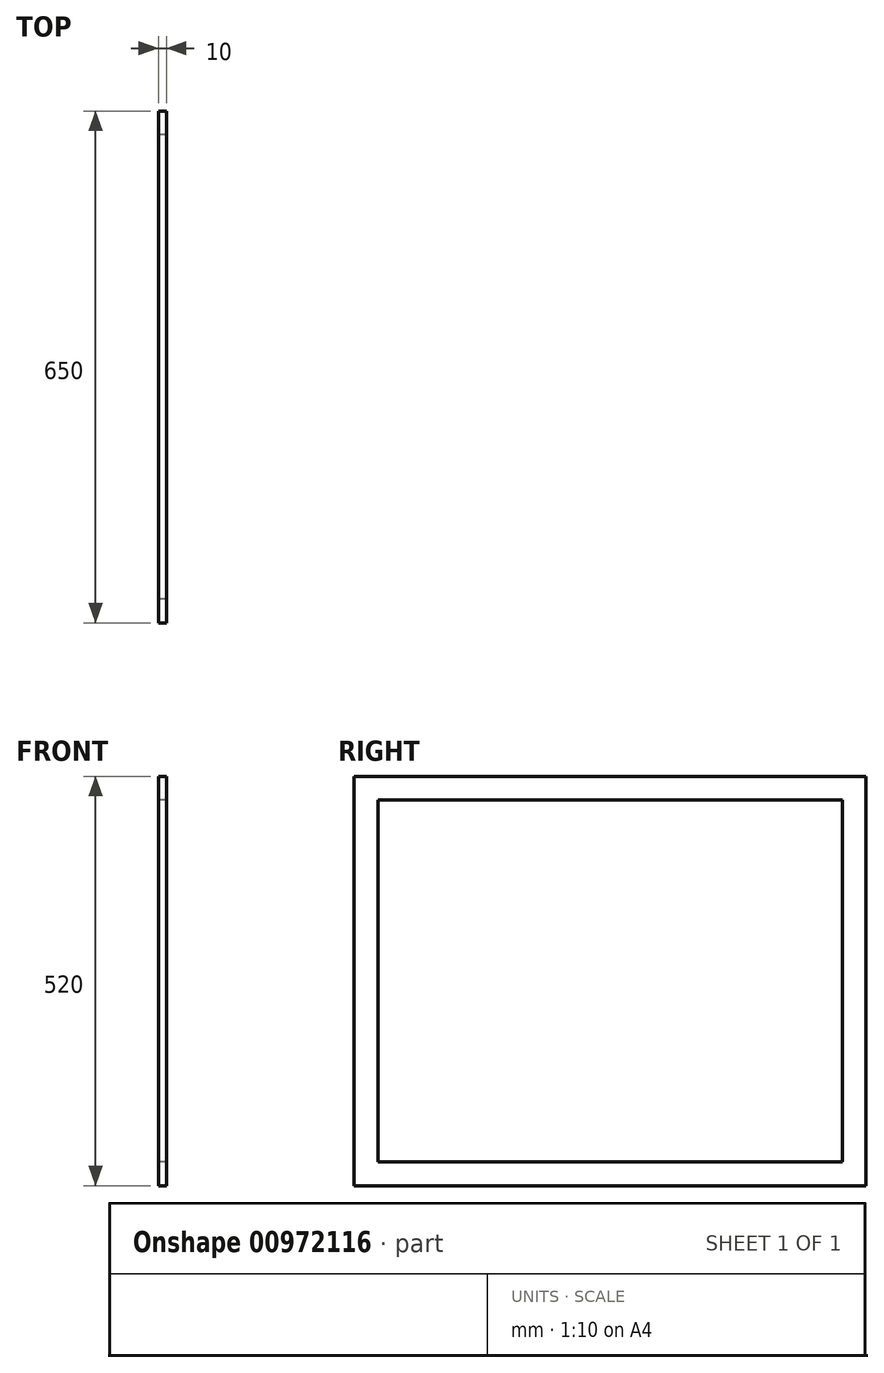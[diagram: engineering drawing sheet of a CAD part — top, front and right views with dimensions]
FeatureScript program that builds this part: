
annotation { "Feature Type Name" : "Feature", "Feature Type Description" : "" }
export const myFeature = defineFeature(function(context is Context, id is Id, definition is map)
    precondition{}
    {
        {
            var Q0;
            Q0=qCreatedBy(makeId("Right.planeOp"),FACE);
            var sketch = newSketch(context, id + "F0", { "sketchPlane" : qUnion([Q0])});
            skLineSegment(sketch, "E0.bottom", {"start": v(-429.77, 280.8) * mm, "end": v(220.23, 280.8) * mm});
            skLineSegment(sketch, "E0.top", {"start": v(-429.77, -239.2) * mm, "end": v(220.23, -239.2) * mm});
            skLineSegment(sketch, "E0.left", {"start": v(-429.77, 280.8) * mm, "end": v(-429.77, -239.2) * mm});
            skLineSegment(sketch, "E0.right", {"start": v(220.23, 280.8) * mm, "end": v(220.23, -239.2) * mm});
            skLineSegment(sketch, "E1.bottom", {"start": v(-399.77, -209.2) * mm, "end": v(190.23, -209.2) * mm});
            skLineSegment(sketch, "E1.top", {"start": v(-399.77, 250.8) * mm, "end": v(190.23, 250.8) * mm});
            skLineSegment(sketch, "E1.left", {"start": v(-399.77, -209.2) * mm, "end": v(-399.77, 250.8) * mm});
            skLineSegment(sketch, "E1.right", {"start": v(190.23, -209.2) * mm, "end": v(190.23, 250.8) * mm});
            skSolve(sketch);
        }
        {
            var Q0;
            Q0=makeQuery(id+"F0.imprint","IMPRINT",FACE,{"disambiguationData":[TD([[makeQuery(id+"F0.imprint","IMPRINT",EDGE,{"derivedFrom":sQuery(id+"F0.wireOp",EDGE,"E0.bottom")}),-1.0]])]});
            extrude(context, id + "F1", {"entities" : qUnion([Q0]), "depth" : 10 * mm, "offsetDistance" : 25 * mm});
        }
    });
